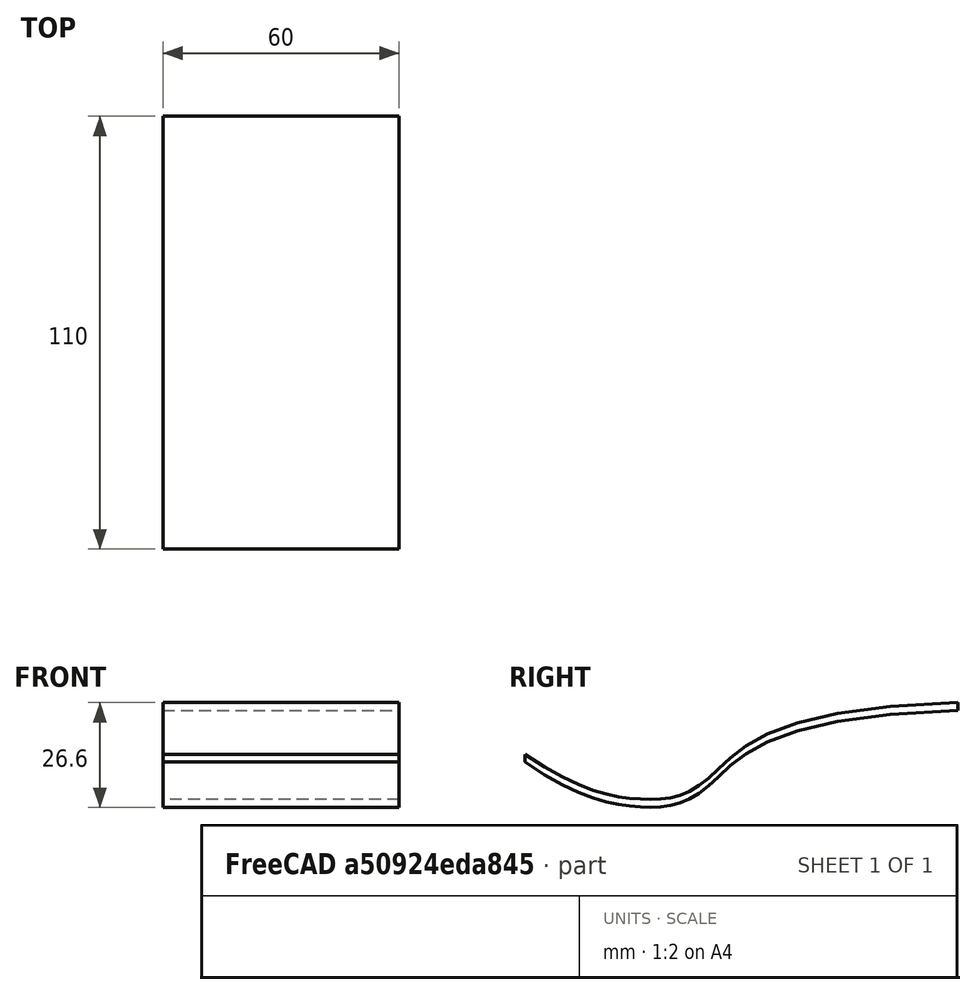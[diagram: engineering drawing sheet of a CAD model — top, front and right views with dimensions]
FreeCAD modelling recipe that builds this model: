
FCSTD DOCUMENT  (FreeCAD 0.20R29177 +426 (Git))
Label: project_17
License: All rights reserved
LicenseURL: https://en.wikipedia.org/wiki/All_rights_reserved
objects: Sketcher::SketchObject×2, Part::Extrusion×2
note: 4 computed .brp shape members not serialized (recipe doc carries the construction recipe); baked Part::Feature solids carry a one-line shape summary decoded from their .brp

FEATURE [Sketcher::SketchObject] Sketch
  FullyConstrained = false
  MapMode = 5
  Placement = pos=(0,0,0) rot=(0.57735,0.57735,0.57735;2.0944rad)
  sketch-geometry (11):
    g0-g5: Circle x6 (B-spline internal-alignment scaffolding for g6; pole/knot coordinates omitted)
    g6: BSplineCurve PolesCount=6 KnotsCount=4 Degree=3 IsPeriodic=0
    g7-g10: GeomPoint x4 (B-spline internal-alignment scaffolding for g6; pole/knot coordinates omitted)
  constraints (4):
    c: Weight(g0) = 1
    c: Equal(g0, g1-g5) x5
    c: InternalAlignment(g0-g5 -> g6) x6
    c: InternalAlignment(g7-g10 -> g6) x4
FEATURE [Part::Extrusion] Extrude
  Base = -> Sketch
  Dir = (0,0,1)
  DirMode = 0
  FaceMakerClass = Part::FaceMakerBullseye
  LengthFwd = 2
  LengthRev = 0
  Solid = false
  Symmetric = false
FEATURE [Part::Extrusion] Extrude001
  Base = -> Extrude
  Dir = (1,0,0)
  DirMode = 0
  FaceMakerClass = Part::FaceMakerBullseye
  LengthFwd = 60
  LengthRev = 0
  Solid = false
  Symmetric = true
FEATURE [Sketcher::SketchObject] Sketch001
  FullyConstrained = false
  Placement = pos=(0,0,23) rot=(0,0,1;0rad)
  sketch-geometry (19):
    g0: LineSegment StartX=-30.6951 StartY=13 StartZ=0 EndX=30.6951 EndY=13 EndZ=0
    g1: ArcOfCircle CenterX=69.5936 CenterY=41.6024 CenterZ=0 NormalX=0 NormalY=0 NormalZ=1 AngleXU=0 Radius=77.3937 StartAngle=2.77039 EndAngle=3.32531
    g2: ArcOfCircle CenterX=-40.7527 CenterY=16.2866 CenterZ=0 NormalX=0 NormalY=0 NormalZ=1 AngleXU=0 Radius=36.0324 StartAngle=6.13661 EndAngle=6.59859
    g3: ArcOfCircle CenterX=8.1487 CenterY=-8.56342 CenterZ=0 NormalX=0 NormalY=0 NormalZ=1 AngleXU=0 Radius=23.6511 StartAngle=2.16573 EndAngle=3.9229
    g4: LineSegment StartX=-8.64345 StartY=-25.2187 StartZ=0 EndX=-6.54228 EndY=-25.2187 EndZ=0
    g5: LineSegment StartX=-6.54228 StartY=-25.2187 StartZ=0 EndX=-6.54228 EndY=-2.8157 EndZ=0
    g6: ArcOfCircle CenterX=-5.70122 CenterY=-3.20254 CenterZ=0 NormalX=0 NormalY=0 NormalZ=1 AngleXU=0 Radius=0.925761 StartAngle=0.431092 EndAngle=2.7105
    g7: LineSegment StartX=-4.86016 StartY=-2.8157 StartZ=0 EndX=-3.21575 EndY=-25.2187 EndZ=0
    g8: LineSegment StartX=-3.21575 StartY=-25.2187 StartZ=0 EndX=-1.35289 EndY=-25.2187 EndZ=0
    g9: LineSegment StartX=-1.35289 StartY=-25.2187 StartZ=0 EndX=-1.35289 EndY=-2.8157 EndZ=0
    g10: ArcOfCircle CenterX=-69.5936 CenterY=41.6024 CenterZ=0 NormalX=0 NormalY=0 NormalZ=1 AngleXU=0 Radius=77.3937 StartAngle=6.09947 EndAngle=6.65439
    g11: ArcOfCircle CenterX=40.7527 CenterY=16.2866 CenterZ=0 NormalX=0 NormalY=0 NormalZ=1 AngleXU=0 Radius=36.0324 StartAngle=2.82619 EndAngle=3.28817
    g12: ArcOfCircle CenterX=-8.1487 CenterY=-8.56342 CenterZ=0 NormalX=0 NormalY=0 NormalZ=1 AngleXU=0 Radius=23.6511 StartAngle=5.50188 EndAngle=7.25905
    g13: LineSegment StartX=8.64345 StartY=-25.2187 StartZ=0 EndX=6.54228 EndY=-25.2187 EndZ=0
    g14: LineSegment StartX=6.54228 StartY=-25.2187 StartZ=0 EndX=6.54228 EndY=-2.8157 EndZ=0
    g15: ArcOfCircle CenterX=5.70122 CenterY=-3.20254 CenterZ=0 NormalX=0 NormalY=0 NormalZ=1 AngleXU=0 Radius=0.925761 StartAngle=0.431092 EndAngle=2.7105
    g16: LineSegment StartX=4.86016 StartY=-2.8157 StartZ=0 EndX=3.21575 EndY=-25.2187 EndZ=0
    g17: LineSegment StartX=3.21575 StartY=-25.2187 StartZ=0 EndX=1.35289 EndY=-25.2187 EndZ=0
    g18: LineSegment StartX=1.35289 StartY=-25.2187 StartZ=0 EndX=1.35289 EndY=-2.8157 EndZ=0
  constraints (38):
    c: Symmetric(g0,g0,g-2)
    c: DistanceY(g-1,g0) = 13
    c: Coincident(g2,g1)
    c: Coincident(g3,g2)
    c: Coincident(g4,g3)
    c: Coincident(g5,g4)
    c: Vertical(g5)
    c: Horizontal(g4)
    c: Coincident(g6,g5)
    c: Coincident(g7,g6)
    c: Coincident(g8,g7)
    c: Horizontal(g8)
    c: Coincident(g9,g8)
    c: Vertical(g9)
    c: Horizontal(g9,g6)
    c: Horizontal(g5,g6)
    c: Horizontal(g4,g7)
    c: Coincident(g11,g10)
    c: Coincident(g12,g11)
    c: Coincident(g13,g12)
    c: Coincident(g14,g13)
    c: Vertical(g14)
    c: Horizontal(g13)
    c: Coincident(g15,g14)
    c: Coincident(g16,g15)
    c: Coincident(g17,g16)
    c: Horizontal(g17)
    c: Coincident(g18,g17)
    c: Vertical(g18)
    c: Horizontal(g11,g2)
    c: Horizontal(g1,g10)
    c: Horizontal(g1,g10)
    c: Horizontal(g15,g14)
    c: Horizontal(g14,g18)
    c: Horizontal(g9,g18)
    c: Horizontal(g17,g13)
    c: Horizontal(g13,g8)
    c: Horizontal(g3,g12)
